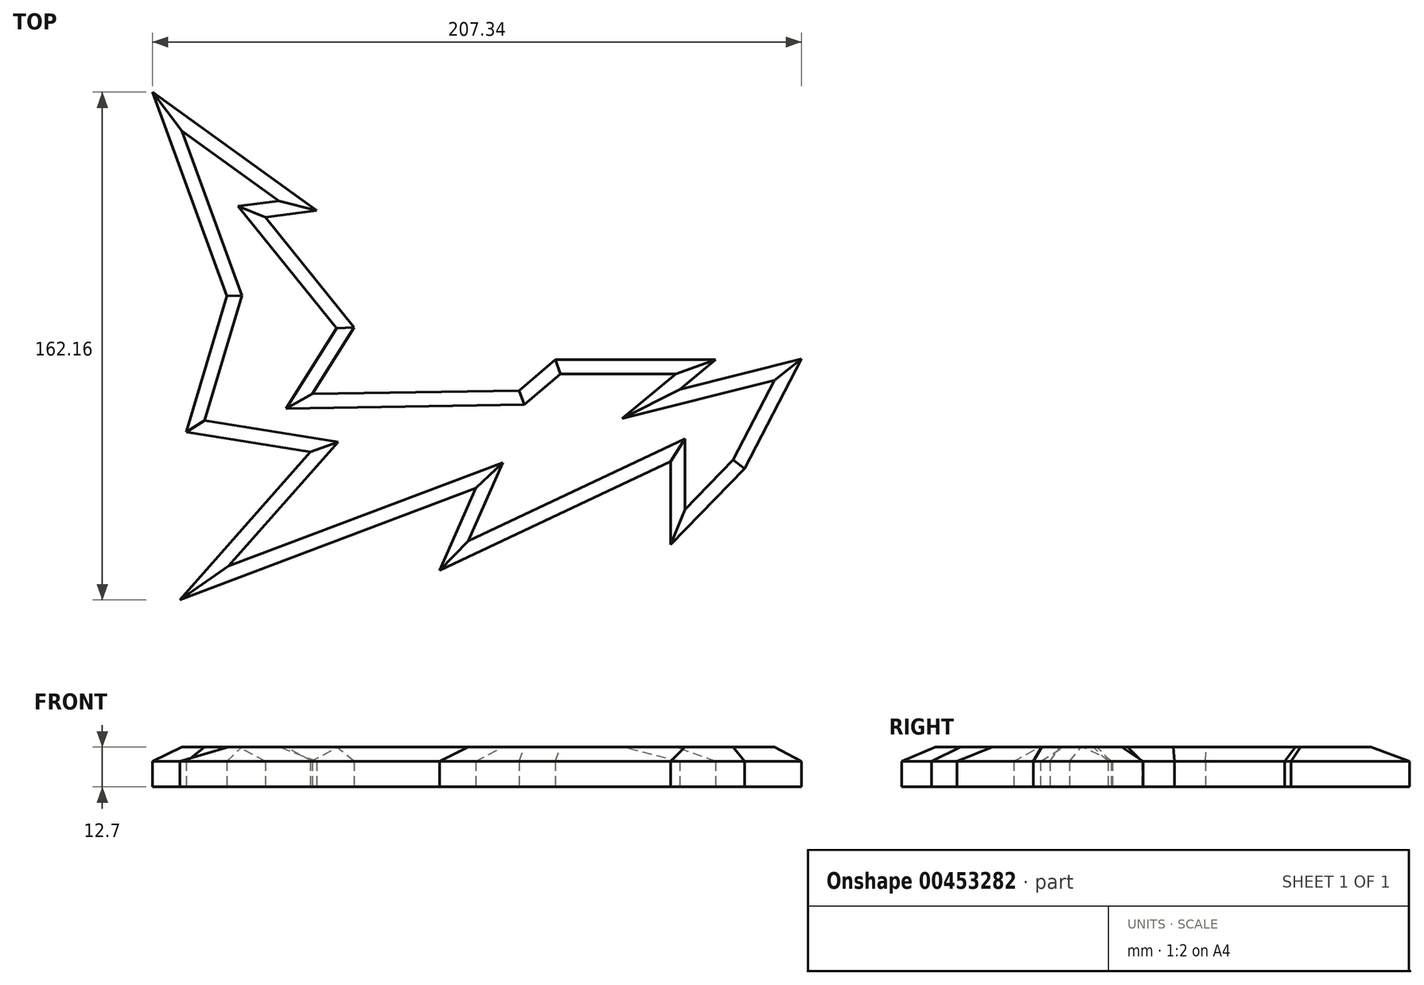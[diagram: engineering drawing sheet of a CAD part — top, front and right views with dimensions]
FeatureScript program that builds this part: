
annotation { "Feature Type Name" : "Feature", "Feature Type Description" : "" }
export const myFeature = defineFeature(function(context is Context, id is Id, definition is map)
    precondition{}
    {
        {
            var Q0;
            Q0=qCreatedBy(makeId("Top.planeOp"),FACE);
            var sketch = newSketch(context, id + "F0", { "sketchPlane" : qUnion([Q0])});
            skLineSegment(sketch, "E0", {"start": v(-180.4, -27.62) * mm, "end": v(-85.83, 8.1) * mm});
            skLineSegment(sketch, "E1", {"start": v(-85.83, 8.1) * mm, "end": v(-97.4, -18.17) * mm});
            skLineSegment(sketch, "E2", {"start": v(-97.4, -18.17) * mm, "end": v(-23.66, 16.66) * mm});
            skLineSegment(sketch, "E3", {"start": v(-23.66, 16.66) * mm, "end": v(-23.66, -9.95) * mm});
            skLineSegment(sketch, "E4", {"start": v(-23.66, -9.95) * mm, "end": v(0, 14.36) * mm});
            skLineSegment(sketch, "E5", {"start": v(18.19, 49.43) * mm, "end": v(-20.69, 39.62) * mm});
            skLineSegment(sketch, "E6", {"start": v(-20.69, 39.62) * mm, "end": v(-9.3, 49.1) * mm});
            skLineSegment(sketch, "E7", {"start": v(-9.3, 49.1) * mm, "end": v(-60.48, 49.1) * mm});
            skLineSegment(sketch, "E8", {"start": v(-60.48, 49.1) * mm, "end": v(-72.06, 39.28) * mm});
            skLineSegment(sketch, "E9", {"start": v(-72.06, 39.28) * mm, "end": v(-138.05, 38.26) * mm});
            skLineSegment(sketch, "E10", {"start": v(-138.05, 38.26) * mm, "end": v(-124.71, 59.46) * mm});
            skLineSegment(sketch, "E11", {"start": v(-124.71, 59.46) * mm, "end": v(-153.08, 94.61) * mm});
            skLineSegment(sketch, "E12", {"start": v(-153.08, 94.61) * mm, "end": v(-136.62, 96.71) * mm});
            skLineSegment(sketch, "E13", {"start": v(-136.62, 96.71) * mm, "end": v(-189.15, 134.54) * mm});
            skLineSegment(sketch, "E14", {"start": v(-189.15, 134.54) * mm, "end": v(-165.34, 69.4) * mm});
            skLineSegment(sketch, "E15", {"start": v(-165.34, 69.4) * mm, "end": v(-178.3, 25.96) * mm});
            skLineSegment(sketch, "E16", {"start": v(-178.3, 25.96) * mm, "end": v(-138.72, 19.66) * mm});
            skLineSegment(sketch, "E17", {"start": v(-138.72, 19.66) * mm, "end": v(-180.4, -27.62) * mm});
            skLineSegment(sketch, "E18", {"start": v(0, 14.36) * mm, "end": v(18.19, 49.43) * mm});
            skSolve(sketch);
        }
        {
            var Q0;
            Q0=makeQuery(id+"F0.imprint","IMPRINT",FACE,{"disambiguationData":[TD([[makeQuery(id+"F0.imprint","IMPRINT",EDGE,{"derivedFrom":sQuery(id+"F0.wireOp",EDGE,"8gzG59oq-OxTQ-FSxx-rdve-sIanwsRWyK6k")}),-1.0]])]});
            var Q1;
            Q1=makeQuery(id+"F0.imprint","IMPRINT",FACE,{"disambiguationData":[TD([[makeQuery(id+"F0.imprint","IMPRINT",EDGE,{"derivedFrom":sQuery(id+"F0.wireOp",EDGE,"RamSxRYM-kuQw-MWln-RZHq-MzstoPWcsuwb")}),1.0]])]});
            var Q2;
            Q2=makeQuery(id+"F0.imprint","IMPRINT",FACE,{"disambiguationData":[TD([[makeQuery(id+"F0.imprint","IMPRINT",EDGE,{"derivedFrom":sQuery(id+"F0.wireOp",EDGE,"E0")}),1.0]])]});
            extrude(context, id + "F1", {"entities" : qUnion([Q0, Q1, Q2]), "depth" : 12.7 * mm});
        }
        {
            var Q0;
            Q0=makeQuery(id+"F1.opExtrude","CAP_FACE",FACE,{"disambiguationData":[OSD([sQuery(id+"F0.wireOp",EDGE,"8gzG59oq-OxTQ-FSxx-rdve-sIanwsRWyK6k"),sQuery(id+"F0.wireOp",EDGE,"RamSxRYM-kuQw-MWln-RZHq-MzstoPWcsuwb"),sQuery(id+"F0.wireOp",EDGE,"xXuEt2Q3-a1Rx-wnKa-WpLo-ZkFXYZCJHJvs"),sQuery(id+"F0.wireOp",EDGE,"E0"),sQuery(id+"F0.wireOp",EDGE,"E1"),sQuery(id+"F0.wireOp",EDGE,"E2"),sQuery(id+"F0.wireOp",EDGE,"E3"),sQuery(id+"F0.wireOp",EDGE,"E4"),sQuery(id+"F0.wireOp",EDGE,"B2qEQKoo-a5le-z1Mv-eolz-fog4vdUYCJJO"),sQuery(id+"F0.wireOp",EDGE,"2wy2kxnH-5XdR-z53D-xJQi-JaYgUHz6AQf5"),sQuery(id+"F0.wireOp",EDGE,"3bj0mjm9-sBFO-ic1M-aFWY-6s8fHODacjw2"),sQuery(id+"F0.wireOp",EDGE,"E54m70q7-mkkY-tm5C-zSwA-sNGJN1V7RjvC"),sQuery(id+"F0.wireOp",EDGE,"L5HIFUve-NZWl-Hr0w-ss2T-ITZYmnr1ZSQo"),sQuery(id+"F0.wireOp",EDGE,"zXPXJxJq-p09I-f5Lf-kzd2-TIBfvAmG105E"),sQuery(id+"F0.wireOp",EDGE,"9APqGg2o-HuPH-3IbR-o6Ck-rxl3kNr2yTHT"),sQuery(id+"F0.wireOp",EDGE,"6viiBPzv-tAvL-oV3w-FkTQ-qZrF4OTuZlP6"),sQuery(id+"F0.wireOp",EDGE,"S6lQaeLE-RXXh-ZGko-gYln-RhRdVj5sKyG0"),sQuery(id+"F0.wireOp",EDGE,"xMENqzmY-AZfS-kdv9-bNZ8-6v2j8awkabzR"),sQuery(id+"F0.wireOp",EDGE,"aUlRPmh3-NiS5-PLdv-aiew-mN4mnFRJ37G4"),sQuery(id+"F0.wireOp",EDGE,"Njx46wXM-JS0p-p438-0PV8-FetzSATfLptO"),sQuery(id+"F0.wireOp",EDGE,"7WGv4O9Y-d7t3-oKnc-eZwR-guaCSuIgJ5RG"),sQuery(id+"F0.wireOp",EDGE,"E5"),sQuery(id+"F0.wireOp",EDGE,"E6"),sQuery(id+"F0.wireOp",EDGE,"E7"),sQuery(id+"F0.wireOp",EDGE,"E8"),sQuery(id+"F0.wireOp",EDGE,"E9")])],"isStart":false});
            chamfer(context, id + "F2", {"entities" : qUnion([Q0]), "width" : 4.57 * mm, "tangentPropagation" : true});
        }
    });
